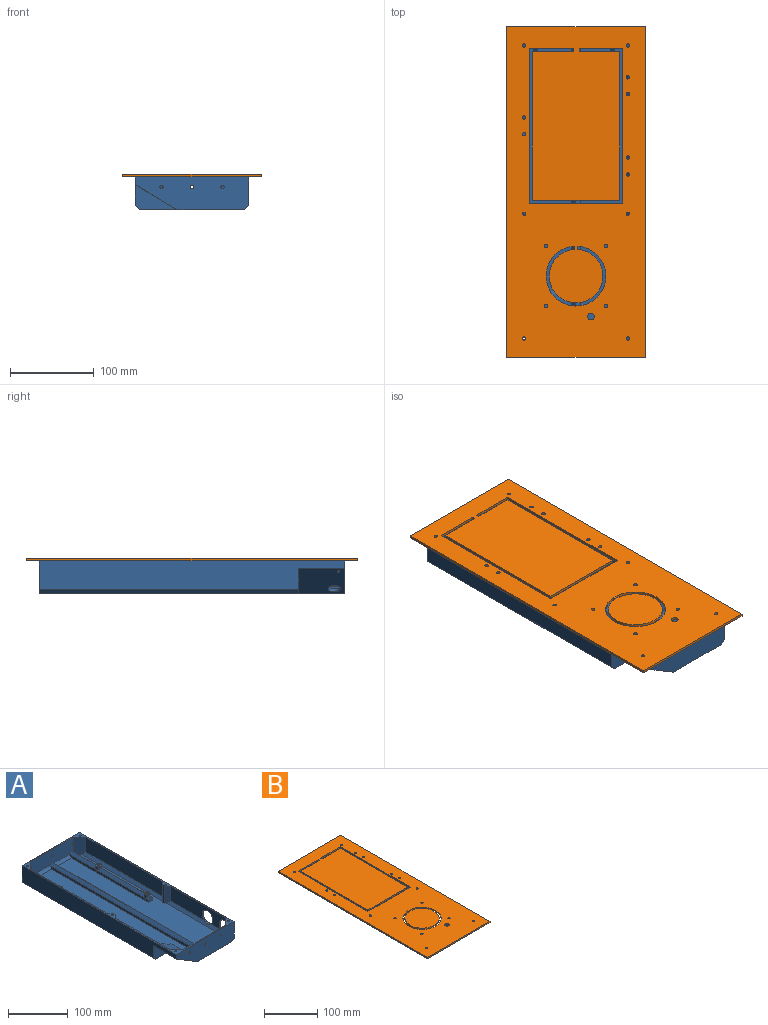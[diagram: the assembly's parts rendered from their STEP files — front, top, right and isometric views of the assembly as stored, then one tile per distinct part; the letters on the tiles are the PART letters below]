
ASSEMBLY  parts=2 mates=1
PART A: 104 faces, bbox 136.4x365.4x39.4 mm
  f0: plane 181.96x30mm, normal (-1,0,0), area 5458.8mm2, adj f1,f20,f83,f100
  f1: plane 191.96x5mm, normal (-0.71,0,0.71), area 1322mm2, adj f0,f8,f83,f100
  f2: plane 181.96x30mm, normal (1,0,0), area 5458.8mm2, adj f3,f20,f82,f103
  f3: plane 191.96x5mm, normal (0.71,0,0.71), area 1322mm2, adj f2,f9,f82,f103
  f4: plane 101x30mm, normal (0,1,0), area 2775.7mm2, adj f20,f30,f58,f61,f72,f73,f77,f78
  f5: plane 136x39mm, normal (0,-1,0), area 4503.8mm2, adj f14,f15,f17,f18,f20,f56,f77,f78
  f6: plane 136x39mm, normal (0,1,0), area 5241.3mm2, adj f15,f17,f18,f20,f56,f57,f74,f75
  f7: plane 101x30mm, normal (0,-1,0), area 2921.7mm2, adj f20,f62,f63,f65,f66,f70,f71,f72
  f8: plane 350x55.5mm, normal (0,0,1), area 17564.1mm2, adj f1,f10,f11,f42,f43,f44,f45,f46
  f9: plane 350x55.5mm, normal (0,0,1), area 15112.7mm2, adj f3,f12,f13,f30,f35,f36,f37,f38
  f10: cylinder r=5mm len=12mm, axis (0,0,-1), area 167.2mm2, adj f8,f24,f42,f44,f69,f70,f71
  f11: cylinder r=5mm len=12mm, axis (0,0,-1), area 167.2mm2, adj f8,f26,f42,f43,f68,f69,f70
  f12: cylinder r=5mm len=12mm, axis (0,0,-1), area 168.7mm2, adj f9,f22,f35,f37,f64,f65,f66
  f13: cylinder r=5mm len=12mm, axis (0,0,-1), area 168.7mm2, adj f9,f28,f35,f36,f64,f66,f67
  f14: plane 55.38x50.38mm, normal (-0.51,0,-0.86), area 3023.6mm2, adj f5,f15,f17,f31,f34,f87
  f15: plane 365x126mm, normal (0,0,-1), area 43515mm2, adj f5,f6,f14,f31,f56,f57
  f16: plane 130.04x30mm, normal (1,0,0), area 2777.5mm2, adj f20,f30,f52,f55,f80,f102
  f17: plane 365x34mm, normal (-1,0,0), area 11035mm2, adj f5,f6,f14,f20,f31,f57
  f18: plane 365x34mm, normal (1,0,0), area 11428.3mm2, adj f5,f6,f20,f32,f33,f56
  f19: plane 130.04x30mm, normal (-1,0,0), area 3135.2mm2, adj f20,f32,f33,f60,f81,f101
  f20: plane 365x136mm, normal (0,0,1), area 3036.7mm2, adj f0,f2,f4,f5,f6,f7,f16,f17
  f21: cylinder r=2mm len=4mm, axis (0,0,-1), area 25.1mm2, adj f22,f41
  f22: plane 10x10mm, normal (0,0,1), area 66mm2, adj f12,f21
  f23: cylinder r=2mm len=4mm, axis (0,0,-1), area 25.1mm2, adj f24,f48
  f24: plane 10x10mm, normal (0,0,1), area 66mm2, adj f10,f23
  f25: cylinder r=2mm len=4mm, axis (0,0,-1), area 25.1mm2, adj f26,f47
  f26: plane 10x10mm, normal (0,0,1), area 66mm2, adj f11,f25
  f27: cylinder r=2mm len=4mm, axis (0,0,-1), area 25.1mm2, adj f28,f40
  f28: plane 10x10mm, normal (0,0,1), area 66mm2, adj f13,f27
  f29: plane 35.27x21.16mm, normal (0,1,0), area 373.3mm2, adj f30,f53,f55
  f30: plane 61.5x48.61mm, normal (0.51,0,0.86), area 2911mm2, adj f4,f9,f16,f29,f34,f53,f55,f58
  f31: plane 50x30mm, normal (0,-1,0), area 737.5mm2, adj f14,f15,f17,f57
  f32: cylinder r=12.5mm len=25mm, axis (1,0,0), area 215.4mm2, adj f18,f19,f60
  f33: cylinder r=12.5mm len=25mm, axis (1,0,0), area 397.9mm2, adj f18,f19,f60,f81,f84,f85,f86
  f34: cylinder r=7.47mm len=14.93mm, axis (-0.51,0,-0.86), area 187.7mm2, adj f14,f30
  f35: plane 113.83x5mm, normal (-1,0,0), area 569.2mm2, adj f9,f12,f13,f64
  f36: plane 7.81x5mm, normal (-1,0,0), area 39mm2, adj f9,f13,f38,f67
  f37: plane 62.95x5mm, normal (-1,0,0), area 304.5mm2, adj f9,f12,f51,f65,f82
  f38: plane 10x10mm, normal (0,-1,0), area 75mm2, adj f9,f36,f39,f66,f67
  f39: plane 187.39x5mm, normal (1,0,0), area 924.5mm2, adj f9,f38,f63,f66
  f40: plane 4x4mm, normal (0,0,1), area 12.6mm2, adj f27
  f41: plane 4x4mm, normal (0,0,1), area 12.6mm2, adj f21
  f42: plane 114.13x5mm, normal (-1,0,0), area 570.7mm2, adj f8,f10,f11,f69
  f43: plane 7.96x5mm, normal (-1,0,0), area 39.8mm2, adj f8,f11,f45,f68
  f44: plane 63.57x5mm, normal (-1,0,0), area 305.3mm2, adj f8,f10,f62,f71
  f45: plane 10x10mm, normal (0,-1,0), area 75mm2, adj f8,f43,f46,f68,f70
  f46: plane 186.87x5mm, normal (1,0,0), area 924.3mm2, adj f8,f45,f59,f70,f83
  f47: plane 4x4mm, normal (0,0,1), area 12.6mm2, adj f25
  f48: plane 4x4mm, normal (0,0,1), area 12.6mm2, adj f23
  f49: plane 360x5mm, normal (-1,0,0), area 1775mm2, adj f9,f58,f63,f73
  f50: plane 360x5mm, normal (1,0,0), area 1775mm2, adj f8,f61,f62,f72
  f51: plane 4.53x4.53mm, normal (0,-0.71,0.71), area 14.5mm2, adj f9,f37,f82
  f52: plane 88.54x5mm, normal (0.71,0,0.71), area 608.4mm2, adj f9,f16,f54,f102
  f53: plane 43.61x5mm, normal (0,0.71,0.71), area 278.9mm2, adj f9,f29,f30,f54
  f54: plane 5x5mm, normal (0.58,0.58,0.58), area 21.7mm2, adj f52,f53,f55
  f55: plane 24.16x5mm, normal (0.71,0.71,0), area 160.3mm2, adj f16,f29,f30,f54
  f56: plane 365x5mm, normal (0.71,0,-0.71), area 2580.9mm2, adj f5,f6,f15,f18
  f57: plane 310x5mm, normal (-0.71,0,-0.71), area 2192mm2, adj f6,f15,f17,f31
  f58: plane 20.23x5mm, normal (0,0.71,0.71), area 113.6mm2, adj f4,f9,f30,f49
  f59: plane 4.48x4.48mm, normal (0,-0.71,0.71), area 14.2mm2, adj f8,f46,f83
  f60: plane 140.04x5mm, normal (-0.71,0,0.71), area 907.3mm2, adj f8,f19,f32,f33,f81,f101
  f61: plane 50.5x5mm, normal (0,0.71,0.71), area 339.4mm2, adj f4,f8,f50,f81
  f62: plane 36.02x5mm, normal (0,-0.71,0.71), area 254.7mm2, adj f7,f8,f44,f50
  f63: plane 35.97x5mm, normal (0,-0.71,0.71), area 254.3mm2, adj f7,f9,f39,f49
  f64: plane 113.83x5mm, normal (-0.71,0,0.71), area 757.2mm2, adj f12,f13,f35,f66
  f65: plane 63.42x5mm, normal (-0.71,0,0.71), area 424.4mm2, adj f7,f12,f37,f66,f82
  f66: plane 187.39x5mm, normal (0.71,0,0.71), area 1215mm2, adj f7,f12,f13,f38,f39,f64,f65,f67
  f67: plane 7.81x5mm, normal (-0.71,0,0.71), area 31.3mm2, adj f13,f36,f38,f66
  f68: plane 7.96x5mm, normal (-0.71,0,0.71), area 31.4mm2, adj f11,f43,f45,f70
  f69: plane 114.13x5mm, normal (-0.71,0,0.71), area 757.4mm2, adj f10,f11,f42,f70
  f70: plane 187.39x5mm, normal (0.71,0,0.71), area 1214.3mm2, adj f7,f10,f11,f45,f46,f68,f69,f71
  f71: plane 63.57x5mm, normal (-0.71,0,0.71), area 424.7mm2, adj f7,f10,f44,f70
  f72: plane 360x5mm, normal (0.71,0,0.71), area 2545.6mm2, adj f4,f7,f50,f73
  f73: plane 360x5mm, normal (-0.71,0,0.71), area 2545.6mm2, adj f4,f7,f49,f72
  f74: cylinder r=2mm len=4mm, axis (0,-1,0), area 33.7mm2, adj f6,f7,f82
  f75: cylinder r=2mm len=4mm, axis (0,-1,0), area 31.4mm2, adj f6,f7
  f76: cylinder r=2mm len=4mm, axis (0,-1,0), area 33.7mm2, adj f6,f7,f83
  f77: cylinder r=2mm len=4mm, axis (0,1,0), area 31.4mm2, adj f4,f5
  f78: cylinder r=2mm len=4mm, axis (0,1,0), area 31.4mm2, adj f4,f5
  f79: cylinder r=2mm len=4mm, axis (0,1,0), area 31.4mm2, adj f4,f5
  f80: plane 15x15mm, normal (0.71,0.71,0), area 219.2mm2, adj f4,f16,f20,f30
  f81: plane 35x15mm, normal (-0.71,0.71,0), area 449.5mm2, adj f4,f8,f19,f20,f33,f60,f61
  f82: plane 35x15mm, normal (0.71,-0.71,0), area 703.9mm2, adj f2,f3,f7,f9,f20,f37,f51,f65
  f83: plane 35x15mm, normal (-0.71,-0.71,0), area 703.8mm2, adj f0,f1,f7,f8,f20,f46,f59,f70
  f84: cylinder r=1.6mm len=25mm, axis (0,0,1), area 202.4mm2, adj f20,f33,f85,f86
  f85: cylinder r=1.6mm len=5.49mm, axis (0,0,1), area 2.4mm2, adj f33,f84,f86
  f86: plane 3.2x2.88mm, normal (0,0,1), area 7.6mm2, adj f33,f84,f85
  f87: cylinder r=1.5mm len=13.5mm, axis (0,0,1), area 118.8mm2, adj f14,f20
  f88: cylinder r=1.6mm len=25mm, axis (0,0,1), area 251.3mm2, adj f20,f89
  f89: plane 3.2x3.2mm, normal (0,0,1), area 8mm2, adj f88
  f90: cylinder r=1.6mm len=25mm, axis (0,0,1), area 251.3mm2, adj f20,f91
  f91: plane 3.2x3.2mm, normal (0,0,1), area 8mm2, adj f90
  f92: plane 35x4mm, normal (1,0,0), area 140mm2, adj f9,f20,f102,f103
  f93: cylinder r=1.6mm len=35mm, axis (0,0,1), area 336.7mm2, adj f20,f94,f95
  f94: plane 3.2x3.1mm, normal (0.71,0,0.71), area 11.3mm2, adj f93,f95
  f95: plane 1.11x0.1mm, normal (0,0,1), area 0.1mm2, adj f93,f94
  f96: plane 35x4mm, normal (-1,0,0), area 140mm2, adj f8,f20,f100,f101
  f97: cylinder r=1.6mm len=35mm, axis (0,0,1), area 336.7mm2, adj f20,f98,f99
  f98: plane 3.2x3.1mm, normal (-0.71,0,0.71), area 11.3mm2, adj f97,f99
  f99: plane 1.11x0.1mm, normal (0,0,1), area 0.1mm2, adj f97,f98
  f100: plane 35x7mm, normal (-0.71,0.71,0), area 328.8mm2, adj f0,f1,f8,f20,f96
  f101: plane 35x7mm, normal (-0.71,-0.71,0), area 328.8mm2, adj f8,f19,f20,f60,f96
  f102: plane 35x7mm, normal (0.71,-0.71,0), area 328.8mm2, adj f9,f16,f20,f52,f92
  f103: plane 35x7mm, normal (0.71,0.71,0), area 328.8mm2, adj f2,f3,f9,f20,f92
PART B: 39 faces, bbox 166x395x3 mm
  f0: plane 166x3mm, normal (0,1,0), area 498mm2, adj f1,f36,f37,f38
  f1: plane 395x3mm, normal (-1,0,0), area 1185mm2, adj f0,f2,f37,f38
  f2: plane 166x3mm, normal (0,-1,0), area 498mm2, adj f1,f36,f37,f38
  f3: plane 3.75x3mm, normal (-1,0,0), area 11.3mm2, adj f4,f17,f37,f38
  f4: cylinder r=32mm len=64mm, axis (0,0,-1), area 592.4mm2, adj f3,f5,f37,f38
  f5: plane 3.76x3mm, normal (1,0,0), area 11.3mm2, adj f4,f17,f37,f38
  f6: plane 178x3mm, normal (1,0,0), area 534mm2, adj f7,f35,f37,f38
  f7: plane 48.57x3mm, normal (0,1,0), area 145.7mm2, adj f6,f8,f37,f38
  f8: plane 3.5x3mm, normal (1,0,0), area 10.5mm2, adj f7,f9,f37,f38
  f9: plane 52.07x3mm, normal (0,-1,0), area 156.2mm2, adj f8,f10,f37,f38
  f10: plane 185x3mm, normal (-1,0,0), area 555mm2, adj f9,f11,f37,f38
  f11: plane 112x3mm, normal (0,1,0), area 336mm2, adj f10,f12,f37,f38
  f12: plane 185x3mm, normal (1,0,0), area 555mm2, adj f11,f13,f37,f38
  f13: plane 53.32x3mm, normal (0,-1,0), area 160mm2, adj f12,f14,f37,f38
  f14: plane 3.5x3mm, normal (-1,0,0), area 10.5mm2, adj f13,f15,f37,f38
  f15: plane 49.82x3mm, normal (0,1,0), area 149.5mm2, adj f14,f16,f37,f38
  f16: plane 178x3mm, normal (-1,0,0), area 534mm2, adj f15,f35,f37,f38
  f17: cylinder r=35.75mm len=71.5mm, axis (0,0,-1), area 663.1mm2, adj f3,f5,f37,f38
  f18: cylinder r=2mm len=4mm, axis (0,0,-1), area 37.7mm2, adj f37,f38
  f19: cylinder r=2mm len=4mm, axis (0,0,-1), area 37.7mm2, adj f37,f38
  f20: cylinder r=2mm len=4mm, axis (0,0,-1), area 37.7mm2, adj f37,f38
  f21: cylinder r=2mm len=4mm, axis (0,0,-1), area 37.7mm2, adj f37,f38
  f22: cylinder r=2mm len=4mm, axis (0,0,-1), area 37.7mm2, adj f37,f38
  f23: cylinder r=2mm len=4mm, axis (0,0,-1), area 37.7mm2, adj f37,f38
  f24: cylinder r=2mm len=4mm, axis (0,0,-1), area 37.7mm2, adj f37,f38
  f25: cylinder r=2mm len=4mm, axis (0,0,-1), area 37.7mm2, adj f37,f38
  f26: cylinder r=2mm len=4mm, axis (0,0,-1), area 37.7mm2, adj f37,f38
  f27: cylinder r=2mm len=4mm, axis (0,0,-1), area 37.7mm2, adj f37,f38
  f28: cylinder r=2mm len=4mm, axis (0,0,-1), area 37.7mm2, adj f37,f38
  f29: cylinder r=2mm len=4mm, axis (0,0,-1), area 37.7mm2, adj f37,f38
  f30: cylinder r=2mm len=4mm, axis (0,0,-1), area 37.7mm2, adj f37,f38
  f31: cylinder r=2mm len=4mm, axis (0,0,-1), area 37.7mm2, adj f37,f38
  f32: cylinder r=2mm len=4mm, axis (0,0,-1), area 37.7mm2, adj f37,f38
  f33: cylinder r=4mm len=8mm, axis (0,0,-1), area 75.4mm2, adj f37,f38
  f34: cylinder r=2mm len=4mm, axis (0,0,-1), area 37.7mm2, adj f37,f38
  f35: plane 105x3mm, normal (0,-1,0), area 315mm2, adj f6,f16,f37,f38
  f36: plane 395x3mm, normal (1,0,0), area 1185mm2, adj f0,f2,f37,f38
  f37: plane 395x166mm, normal (0,0,1), area 62527.1mm2, adj f0,f1,f2,f3,f4,f5,f6,f7
  f38: plane 395x166mm, normal (0,0,-1), area 62527.1mm2, adj f0,f1,f2,f3,f4,f5,f6,f7
PLACE A t=(111.17,-47.92,17.27)mm
PLACE B t=(440.85,-47.89,56.27)mm
MATE fastened B.f21 <-> A.f84  axis (0,0,-1) through (-212.2,-308.8,56.27)mm
